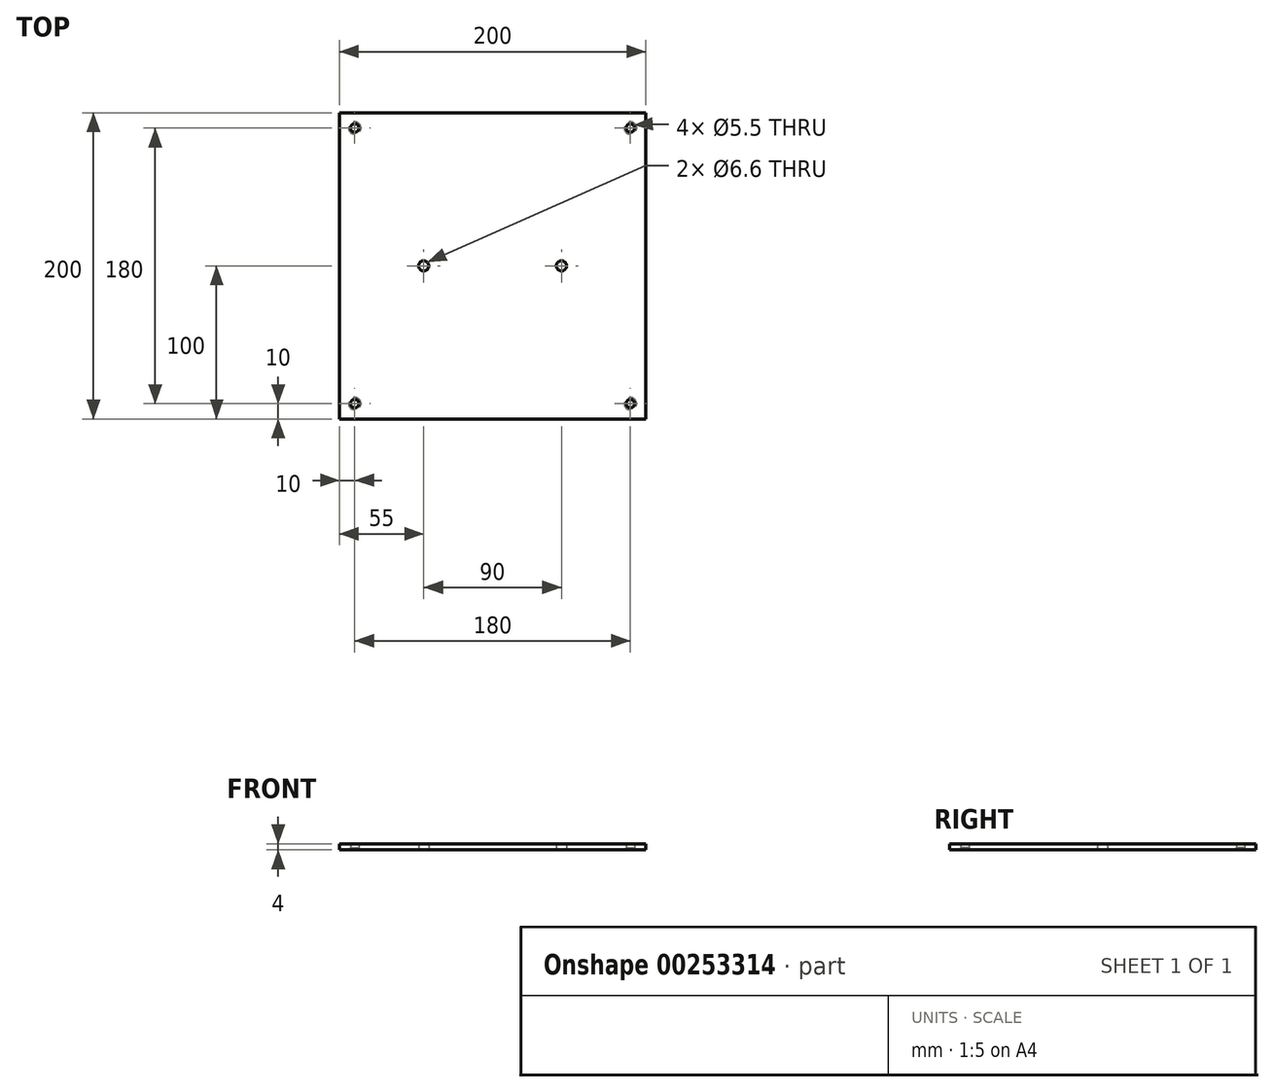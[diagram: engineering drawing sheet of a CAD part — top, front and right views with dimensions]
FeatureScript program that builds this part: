
annotation { "Feature Type Name" : "Feature", "Feature Type Description" : "" }
export const myFeature = defineFeature(function(context is Context, id is Id, definition is map)
    precondition{}
    {
        {
            var Q0;
            Q0=qCreatedBy(makeId("Top.planeOp"),FACE);
            var sketch = newSketch(context, id + "F0", { "sketchPlane" : qUnion([Q0])});
            skLineSegment(sketch, "E0.bottom", {"start": v(100, 100) * mm, "end": v(-100, 100) * mm});
            skLineSegment(sketch, "E0.top", {"start": v(100, -100) * mm, "end": v(-100, -100) * mm});
            skLineSegment(sketch, "E0.left", {"start": v(100, 100) * mm, "end": v(100, -100) * mm});
            skLineSegment(sketch, "E0.right", {"start": v(-100, 100) * mm, "end": v(-100, -100) * mm});
            skPoint(sketch, "E0.middle", {"position": v(0, 0) * mm});
            skPoint(sketch, "E1", {"position": v(-90, 90) * mm});
            skPoint(sketch, "E2.MirrorP", {"position": v(90, 90) * mm});
            skPoint(sketch, "E3.MirrorP", {"position": v(-90, -90) * mm});
            skPoint(sketch, "E4.MirrorP", {"position": v(90, -90) * mm});
            skPoint(sketch, "E5", {"position": v(-45, 0) * mm});
            skPoint(sketch, "E6.MirrorP", {"position": v(45, 0) * mm});
            skSolve(sketch);
        }
        {
            var Q0;
            Q0=makeQuery(id+"F0.imprint","IMPRINT",FACE,{"disambiguationData":[TD([[makeQuery(id+"F0.imprint","IMPRINT",EDGE,{"derivedFrom":sQuery(id+"F0.wireOp",EDGE,"E0.bottom")}),1.0]])]});
            extrude(context, id + "F1", {"entities" : qUnion([Q0]), "depth" : 4 * mm});
        }
        {
            var Q0;
            Q0=sQuery(id+"F0.wireOp",VERTEX,"E3.MirrorP");
            var Q1;
            Q1=sQuery(id+"F0.wireOp",VERTEX,"E4.MirrorP");
            var Q2;
            Q2=sQuery(id+"F0.wireOp",VERTEX,"E2.MirrorP");
            var Q3;
            Q3=sQuery(id+"F0.wireOp",VERTEX,"E1");
            var Q4;
            Q4=makeQuery(id+"F1.opExtrude","SWEPT_BODY",BODY,{"disambiguationData":[OSD([sQuery(id+"F0.wireOp",EDGE,"E0.bottom"),sQuery(id+"F0.wireOp",EDGE,"E0.top"),sQuery(id+"F0.wireOp",EDGE,"E0.left"),sQuery(id+"F0.wireOp",EDGE,"E0.right")])]});
            hole(context, id + "F2", {"style" : HoleStyle.C_SINK, "endStyle" : HoleEndStyle.THROUGH, "oppositeDirection" : true, "holeDiameter" : 5.5 * mm, "cSinkDiameter" : 8 * mm, "cSinkAngle" : 90 * degree, "tappedDepth" : 12 * mm, "tapClearance" : 3, "locations" : qUnion([Q0, Q1, Q2, Q3]), "scope" : qUnion([Q4])});
        }
        {
            var Q0;
            Q0=sQuery(id+"F0.wireOp",VERTEX,"E6.MirrorP");
            var Q1;
            Q1=sQuery(id+"F0.wireOp",VERTEX,"E5");
            var Q2;
            Q2=makeQuery(id+"F1.opExtrude","SWEPT_BODY",BODY,{"disambiguationData":[OSD([sQuery(id+"F0.wireOp",EDGE,"E0.bottom"),sQuery(id+"F0.wireOp",EDGE,"E0.top"),sQuery(id+"F0.wireOp",EDGE,"E0.left"),sQuery(id+"F0.wireOp",EDGE,"E0.right")])]});
            hole(context, id + "F3", {"style" : HoleStyle.SIMPLE, "endStyle" : HoleEndStyle.THROUGH, "oppositeDirection" : true, "standardTappedOrClearance" : lookupTablePath({ "standard" : "ISO", "fit" : "Normal", "size" : "M6", "type" : "Clearance" }), "standardBlindInLast" : lookupTablePath({ "fit" : "Standard", "standard" : "ISO", "size" : "M6", "type" : "Clearance" }), "holeDiameter" : 6.6 * mm, "tappedDepth" : 12 * mm, "tapClearance" : 3, "locations" : qUnion([Q0, Q1]), "scope" : qUnion([Q2])});
        }
    });
